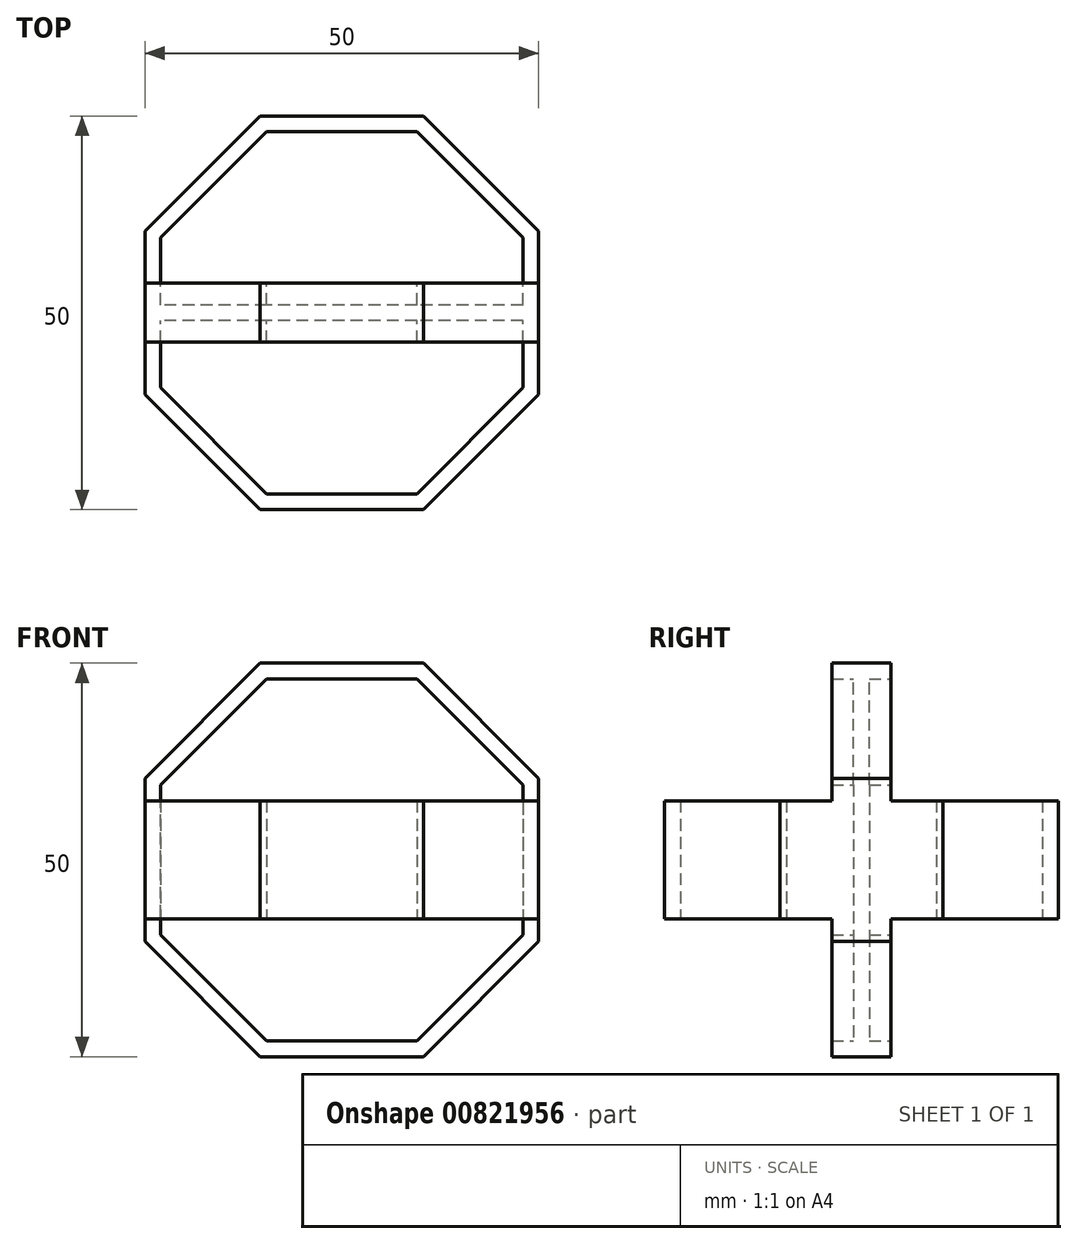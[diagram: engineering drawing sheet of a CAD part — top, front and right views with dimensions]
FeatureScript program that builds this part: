
annotation { "Feature Type Name" : "Feature", "Feature Type Description" : "" }
export const myFeature = defineFeature(function(context is Context, id is Id, definition is map)
    precondition{}
    {
        {
            assignVariable(context, id + "F0", {"name" : "thickness", "anyValue" : 2});
        }
        {
            assignVariable(context, id + "F1", {"name" : "fatness", "anyValue" : 7.5});
        }
        {
            var Q0;
            Q0=qCreatedBy(makeId("Top.planeOp"),FACE);
            var sketch = newSketch(context, id + "F2", { "sketchPlane" : qUnion([Q0])});
            skCircle(sketch, "E0.cCircle", {"center": v(0, 0) * mm, "radius": 25 * mm, "construction": true});
            skLineSegment(sketch, "E0.0", {"start": v(-10.36, 25) * mm, "end": v(10.36, 25) * mm});
            skLineSegment(sketch, "E0.1", {"start": v(10.36, 25) * mm, "end": v(25, 10.36) * mm});
            skLineSegment(sketch, "E0.2", {"start": v(25, 10.36) * mm, "end": v(25, -10.36) * mm});
            skLineSegment(sketch, "E0.3", {"start": v(25, -10.36) * mm, "end": v(10.36, -25) * mm});
            skLineSegment(sketch, "E0.4", {"start": v(10.36, -25) * mm, "end": v(-10.36, -25) * mm});
            skLineSegment(sketch, "E0.5", {"start": v(-10.36, -25) * mm, "end": v(-25, -10.36) * mm});
            skLineSegment(sketch, "E0.6", {"start": v(-25, -10.36) * mm, "end": v(-25, 10.36) * mm});
            skLineSegment(sketch, "E0.7", {"start": v(-25, 10.36) * mm, "end": v(-10.36, 25) * mm});
            skPoint(sketch, "E0.0.midPoint", {"position": v(0, 25) * mm});
            skLineSegment(sketch, "E1", {"start": v(0, 0) * mm, "end": v(0, 3.4) * mm, "construction": true});
            skCircle(sketch, "E2.cCircle", {"center": v(0, 0) * mm, "radius": 23 * mm, "construction": true});
            skLineSegment(sketch, "E2.0", {"start": v(-9.53, 23) * mm, "end": v(9.53, 23) * mm});
            skLineSegment(sketch, "E2.1", {"start": v(9.53, 23) * mm, "end": v(23, 9.53) * mm});
            skLineSegment(sketch, "E2.2", {"start": v(23, 9.53) * mm, "end": v(23, -9.53) * mm});
            skLineSegment(sketch, "E2.3", {"start": v(23, -9.53) * mm, "end": v(9.53, -23) * mm});
            skLineSegment(sketch, "E2.4", {"start": v(9.53, -23) * mm, "end": v(-9.53, -23) * mm});
            skLineSegment(sketch, "E2.5", {"start": v(-9.53, -23) * mm, "end": v(-23, -9.53) * mm});
            skLineSegment(sketch, "E2.6", {"start": v(-23, -9.53) * mm, "end": v(-23, 9.53) * mm});
            skLineSegment(sketch, "E2.7", {"start": v(-23, 9.53) * mm, "end": v(-9.53, 23) * mm});
            skPoint(sketch, "E2.0.midPoint", {"position": v(0, 23) * mm});
            skSolve(sketch);
        }
        {
            var Q0;
            Q0=makeQuery(id+"F2.imprint","IMPRINT",FACE,{"disambiguationData":[TD([[makeQuery(id+"F2.imprint","IMPRINT",EDGE,{"derivedFrom":sQuery(id+"F2.wireOp",EDGE,"E0.0")}),-1.0]])]});
            extrude(context, id + "F3", {"entities" : qUnion([Q0]), "endBound" : BoundingType.SYMMETRIC, "depth" : getVariable(context, 'fatness') * 2 * mm, "offsetDistance" : 25 * mm});
        }
        {
            var Q0;
            Q0=qCreatedBy(makeId("Front.planeOp"),FACE);
            var sketch = newSketch(context, id + "F4", { "sketchPlane" : qUnion([Q0])});
            skCircle(sketch, "E3.cCircle", {"center": v(0, 0) * mm, "radius": 25 * mm, "construction": true});
            skLineSegment(sketch, "E3.0", {"start": v(25, 10.36) * mm, "end": v(25, -10.36) * mm});
            skLineSegment(sketch, "E3.1", {"start": v(25, -10.36) * mm, "end": v(10.36, -25) * mm});
            skLineSegment(sketch, "E3.2", {"start": v(10.36, -25) * mm, "end": v(-10.36, -25) * mm});
            skLineSegment(sketch, "E3.3", {"start": v(-10.36, -25) * mm, "end": v(-25, -10.36) * mm});
            skLineSegment(sketch, "E3.4", {"start": v(-25, -10.36) * mm, "end": v(-25, 10.36) * mm});
            skLineSegment(sketch, "E3.5", {"start": v(-25, 10.36) * mm, "end": v(-10.36, 25) * mm});
            skLineSegment(sketch, "E3.6", {"start": v(-10.36, 25) * mm, "end": v(10.36, 25) * mm});
            skLineSegment(sketch, "E3.7", {"start": v(10.36, 25) * mm, "end": v(25, 10.36) * mm});
            skPoint(sketch, "E3.0.midPoint", {"position": v(25, 0) * mm});
            skLineSegment(sketch, "E4", {"start": v(0, 0) * mm, "end": v(0, 9.48) * mm, "construction": true});
            skCircle(sketch, "E5.cCircle", {"center": v(0, 0) * mm, "radius": 23 * mm, "construction": true});
            skLineSegment(sketch, "E5.0", {"start": v(9.53, -23) * mm, "end": v(-9.53, -23) * mm});
            skLineSegment(sketch, "E5.1", {"start": v(-9.53, -23) * mm, "end": v(-23, -9.53) * mm});
            skLineSegment(sketch, "E5.2", {"start": v(-23, -9.53) * mm, "end": v(-23, 9.53) * mm});
            skLineSegment(sketch, "E5.3", {"start": v(-23, 9.53) * mm, "end": v(-9.53, 23) * mm});
            skLineSegment(sketch, "E5.4", {"start": v(-9.53, 23) * mm, "end": v(9.53, 23) * mm});
            skLineSegment(sketch, "E5.5", {"start": v(9.53, 23) * mm, "end": v(23, 9.53) * mm});
            skLineSegment(sketch, "E5.6", {"start": v(23, 9.53) * mm, "end": v(23, -9.53) * mm});
            skLineSegment(sketch, "E5.7", {"start": v(23, -9.53) * mm, "end": v(9.53, -23) * mm});
            skPoint(sketch, "E5.0.midPoint", {"position": v(0, -23) * mm});
            skSolve(sketch);
        }
        {
            var Q0;
            Q0=makeQuery(id+"F4.imprint","IMPRINT",FACE,{"disambiguationData":[TD([[makeQuery(id+"F4.imprint","IMPRINT",EDGE,{"derivedFrom":sQuery(id+"F4.wireOp",EDGE,"E3.0")}),-1.0]])]});
            extrude(context, id + "F5", {"entities" : qUnion([Q0]), "operationType" : NewBodyOperationType.ADD, "endBound" : BoundingType.SYMMETRIC, "depth" : getVariable(context, 'fatness') * mm, "offsetDistance" : 25 * mm});
        }
        {
            var Q0;
            Q0 = qSketchRegion(id + "F4", true);
            var Q1;
            Q1=makeQuery(id+"F4.imprint","IMPRINT",FACE,{"disambiguationData":[TD([[makeQuery(id+"F4.imprint","IMPRINT",EDGE,{"derivedFrom":sQuery(id+"F4.wireOp",EDGE,"E5.0")}),-1.0]])]});
            extrude(context, id + "F6", {"entities" : qUnion([Q0, Q1]), "operationType" : NewBodyOperationType.ADD, "endBound" : BoundingType.SYMMETRIC, "depth" : (getVariable(context, 'thickness')) * mm, "offsetDistance" : 25 * mm});
        }
    });
